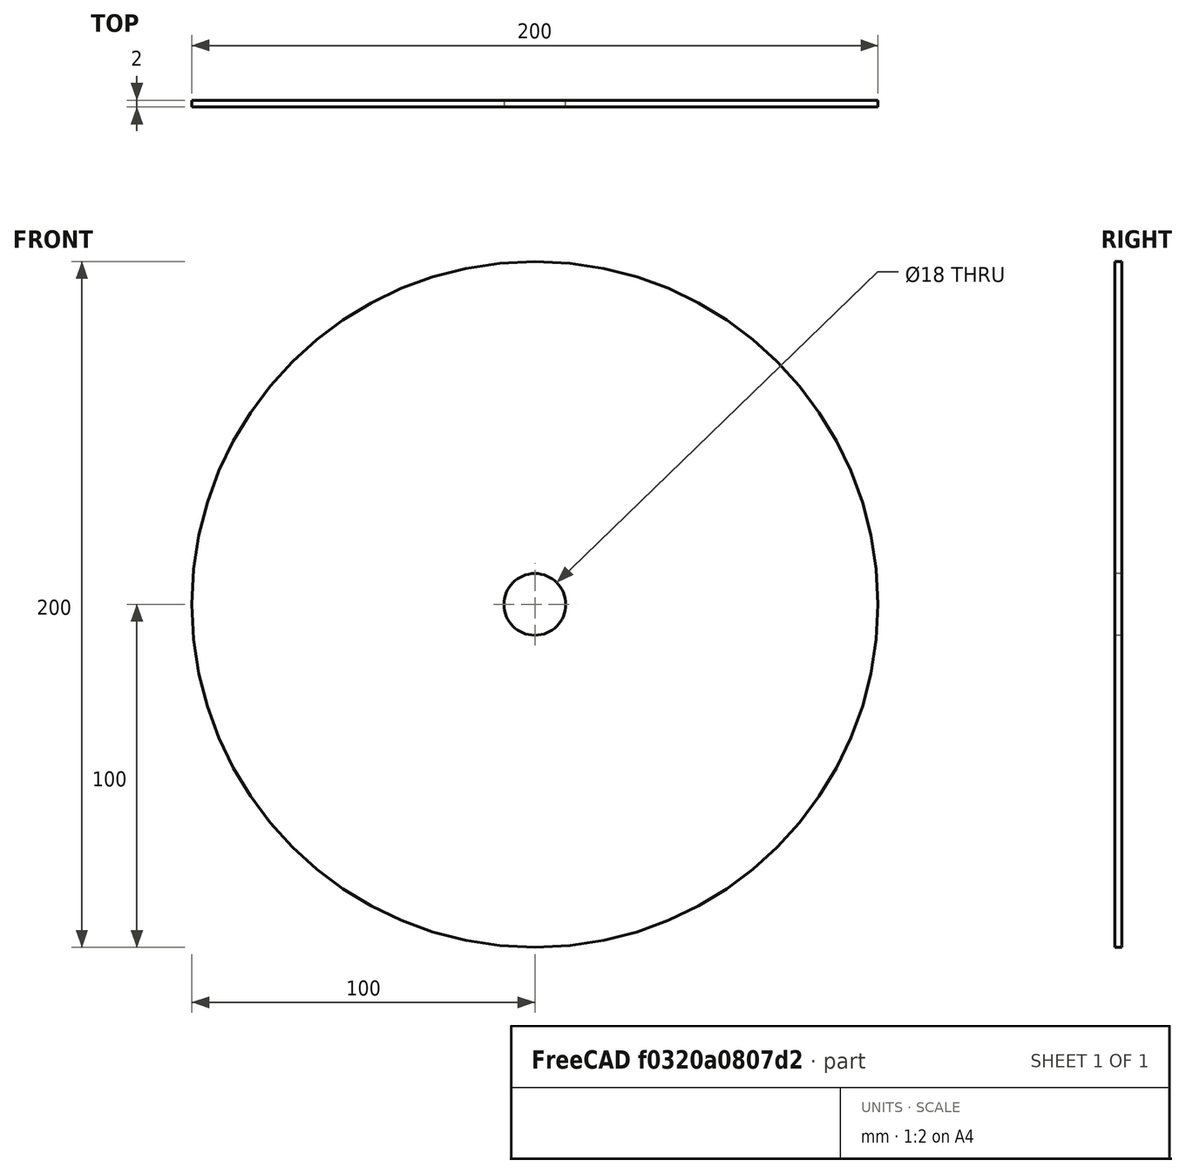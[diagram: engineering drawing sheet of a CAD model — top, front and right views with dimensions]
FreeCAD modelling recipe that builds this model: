
FCSTD DOCUMENT  (FreeCAD 0.21R33771 (Git))
Label: SBHH
License: All rights reserved
LicenseURL: https://en.wikipedia.org/wiki/All_rights_reserved
objects: Sketcher::SketchObject×2, TechDraw::DrawSVGTemplate×2, TechDraw::DrawViewPart×2, TechDraw::DrawPage×2, TechDraw::DrawViewDimExtent×2, Spreadsheet::Sheet×1, PartDesign::Pad×1, PartDesign::Pocket×1, PartDesign::Body×1
note: 9 computed .brp shape members not serialized (recipe doc carries the construction recipe); baked Part::Feature solids carry a one-line shape summary decoded from their .brp

FEATURE [Spreadsheet::Sheet] Spreadsheet  label="specification"
  cells = A1='Name ; B1(name)='Sägeblatt; A2='Beschreibung ; B2(description)='Sägeblatt for Harthölzer; A3='Typ ; B3(type)='SBHH; A4='Stammblattbreite (mm) ; B4(stammblattbreite)=2; A5='Plattensitzhöhe (mm) ; B5(plattensitzhoehe)=3; A6='Plattensitzlänge (mm) ; B6(plattensitzlaenge)=3; A7='Plattensitzwinkel (°) ; B7(plattensitzwinkel)=30; A8='Schnittbreite (mm) ; B8(schnittbreite)=5; A9='Außendurchmesser (mm) ; B9(aussendurchmesser)=200; A10='Bohrungsdurchmesser (mm) ; B10(bohrungsdurchmesser)=18; A11='Zähnezahl ; B11(zaehnezahl)=80
FEATURE [Sketcher::SketchObject] Sketch
  FullyConstrained = true
  MapMode = 5
  Placement = pos=(0,0,0) rot=(1,0,0;1.5708rad)
  Support = -> [XZ_Plane]
  expr: Constraints[1] = Spreadsheet.aussendurchmesser
  sketch-geometry (1):
    g0: Circle CenterX=0 CenterY=0 CenterZ=0 NormalX=0 NormalY=0 NormalZ=1 AngleXU=0 Radius=100
  constraints (2):
    c: Coincident(g0,g-1)
    c: Diameter(g0) = 200
FEATURE [PartDesign::Pad] Pad
  Direction = (0,-1,-2e-16)
  Length = 2
  Length2 = 10
  Placement = pos=(0,0,0) rot=(1,0,0;1.5708rad)
  Profile = -> Sketch
  ReferenceAxis = -> Sketch [N_Axis]
  Type = 0
  expr: Length = Spreadsheet.stammblattbreite
FEATURE [Sketcher::SketchObject] Sketch001
  FullyConstrained = true
  MapMode = 5
  Placement = pos=(0,0,0) rot=(1,0,0;1.5708rad)
  Support = -> [XZ_Plane]
  expr: Constraints[1] = Spreadsheet.bohrungsdurchmesser
  sketch-geometry (1):
    g0: Circle CenterX=0 CenterY=0 CenterZ=0 NormalX=0 NormalY=0 NormalZ=1 AngleXU=0 Radius=9
  constraints (2):
    c: Coincident(g0,g-1)
    c: Diameter(g0) = 18
FEATURE [PartDesign::Pocket] Pocket
  BaseFeature = -> Pad
  Direction = (0,1,2e-16)
  Length = 5
  Length2 = 5
  Midplane = true
  Placement = pos=(0,0,0) rot=(1,0,0;1.5708rad)
  Profile = -> Sketch001
  ReferenceAxis = -> Sketch001 [N_Axis]
  Type = 1
FEATURE [PartDesign::Body] Body  label="Körper"
  Group = -> [Sketch,Pad,Sketch001,Pocket]
  Origin = -> Origin
  Tip = -> Pocket
FEATURE [TechDraw::DrawSVGTemplate] Template
  Height = 841
  Orientation = 1
  Template = C:/Program Files/FreeCAD 0.21/data/Mod/TechDraw/Templates/A0_Landscape_blank.svg
  Width = 1189
FEATURE [TechDraw::DrawViewPart] View
  CoarseView = false
  Direction = (0,-1,0)
  Focus = 100
  HardHidden = false
  IsoCount = 0
  IsoHidden = false
  IsoVisible = false
  LockPosition = false
  Perspective = false
  Rotation = 0
  ScaleType = 0
  ScrubCount = 0
  SeamHidden = false
  SeamVisible = false
  SmoothHidden = false
  SmoothVisible = true
  Source = -> [Body]
  X = 594.5
  XDirection = (1,0,0)
  Y = 420.5
FEATURE [TechDraw::DrawPage] Page  label="dxfexport"
  KeepUpdated = true
  NextBalloonIndex = 1
  ProjectionType = 0
  Template = -> Template
  Views = -> [View]
FEATURE [TechDraw::DrawSVGTemplate] Template001
  EditableTexts = Designed_by_Name=Designed by Name; Drawing_number=Drawing number; FC-Date=Date; FC-SC=Scale; FC-SH=Sheet; FC-Title=Title; Subtitle=Subtitle; Weight=Weight
  Height = 210
  Orientation = 1
  Template = C:/Program Files/FreeCAD 0.21/data/Mod/TechDraw/Templates/A4_LandscapeTD.svg
  Width = 297
FEATURE [TechDraw::DrawViewPart] View001
  CoarseView = false
  Direction = (0,-1,0)
  Focus = 100
  HardHidden = false
  IsoCount = 0
  IsoHidden = false
  IsoVisible = false
  LockPosition = false
  Perspective = false
  Rotation = 0
  Scale = 0.5
  ScaleType = 2
  ScrubCount = 0
  SeamHidden = false
  SeamVisible = false
  SmoothHidden = false
  SmoothVisible = true
  Source = -> [Body]
  X = 148.5
  XDirection = (1,0,0)
  Y = 105
FEATURE [TechDraw::DrawViewDimExtent] DimExtent
  AngleOverride = false
  Arbitrary = false
  ArbitraryTolerances = false
  DirExtent = 0
  EqualTolerance = true
  ExtensionAngle = 0
  FormatSpec = %.2w
  FormatSpecOverTolerance = %+.2w
  FormatSpecUnderTolerance = %+.2w
  Inverted = false
  LineAngle = 0
  LockPosition = false
  MeasureType = 1
  OverTolerance = 0
  References2D = -> [View001]
  Rotation = 0
  ScaleType = 0
  Source = -> [View001]
  TheoreticalExact = false
  Type = 1
  UnderTolerance = 0
  X = -0.897436
  Y = 70.8974
FEATURE [TechDraw::DrawViewDimExtent] DimExtent001
  AngleOverride = false
  Arbitrary = false
  ArbitraryTolerances = false
  DirExtent = 0
  EqualTolerance = true
  ExtensionAngle = 0
  FormatSpec = %.2w
  FormatSpecOverTolerance = %+.2w
  FormatSpecUnderTolerance = %+.2w
  Inverted = false
  LineAngle = 0
  LockPosition = false
  MeasureType = 1
  OverTolerance = 0
  References2D = -> [View001]
  Rotation = 0
  ScaleType = 0
  Source = -> [View001]
  TheoreticalExact = false
  Type = 1
  UnderTolerance = 0
  X = 0
  Y = -7.17949
FEATURE [TechDraw::DrawPage] Page001  label="technical-drawing"
  KeepUpdated = true
  NextBalloonIndex = 1
  ProjectionType = 0
  Template = -> Template001
  Views = -> [View001,DimExtent,DimExtent001]
